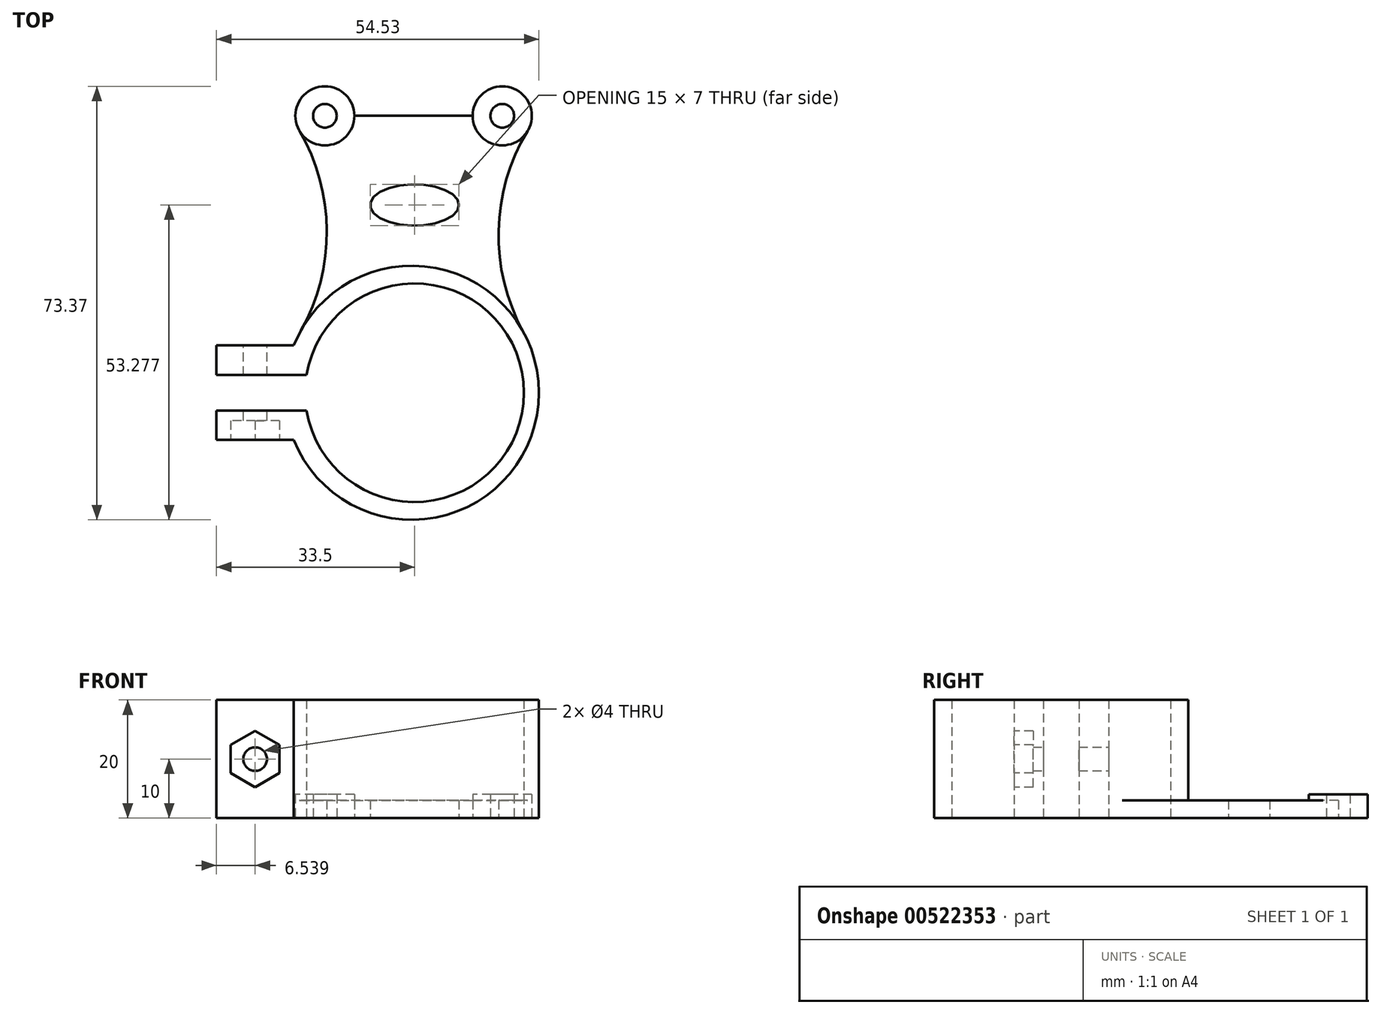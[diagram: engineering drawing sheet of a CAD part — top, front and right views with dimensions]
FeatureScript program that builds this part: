
annotation { "Feature Type Name" : "Feature", "Feature Type Description" : "" }
export const myFeature = defineFeature(function(context is Context, id is Id, definition is map)
    precondition{}
    {
        {
            var Q0;
            Q0=qCreatedBy(makeId("Top.planeOp"),FACE);
            var sketch = newSketch(context, id + "F0", { "sketchPlane" : qUnion([Q0])});
            skArc(sketch, "E0", {"start": v(-18.26, -2.84) * mm, "mid": v(18.5, 0.16) * mm, "end": v(-18.26, 3.16) * mm});
            skLineSegment(sketch, "E1", {"start": v(0, 0) * mm, "end": v(0, -51.02) * mm, "construction": true});
            skLineSegment(sketch, "E2", {"start": v(-15.16, 47.03) * mm, "end": v(14.84, 47.03) * mm});
            skCircle(sketch, "E3", {"center": v(-15.16, 47.03) * mm, "radius": 2 * mm});
            skCircle(sketch, "E4", {"center": v(14.84, 47.03) * mm, "radius": 2 * mm});
            skCircle(sketch, "E5.0", {"center": v(14.84, 47.03) * mm, "radius": 5 * mm});
            skCircle(sketch, "E6.0", {"center": v(-15.16, 47.03) * mm, "radius": 5 * mm});
            skPoint(sketch, "E7.orphan", {"position": v(0, 15) * mm});
            skPoint(sketch, "E8.end.orphan", {"position": v(0, -15) * mm});
            skPoint(sketch, "E9.orphan", {"position": v(0, 21.5) * mm});
            skPoint(sketch, "E10.orphan", {"position": v(0, -21.34) * mm});
            skPoint(sketch, "E11.orphan", {"position": v(-20.16, 47.03) * mm});
            skPoint(sketch, "E12.orphan", {"position": v(19.84, 47.03) * mm});
            skEllipse(sketch, "E13", {"center": v(0, 31.94) * mm, "majorRadius": 7.5 * mm, "minorRadius": 3.5 * mm, "majorAxis": v(1, 0)});
            skLineSegment(sketch, "E14.bottom", {"start": v(-33.5, -5.84) * mm, "end": v(-33.5, -2.84) * mm});
            skPoint(sketch, "E14.middle", {"position": v(-21.5, 0) * mm});
            skLineSegment(sketch, "E15.0", {"start": v(-33.5, 3.16) * mm, "end": v(-21.29, 3.16) * mm});
            skLineSegment(sketch, "E16.0", {"start": v(-33.5, -2.84) * mm, "end": v(-21.29, -2.84) * mm});
            skPoint(sketch, "E17.trimOffspring.end.orphan", {"position": v(-9.5, -6.16) * mm});
            skPoint(sketch, "E18.trimOffspring.end.orphan", {"position": v(-9.5, 5.84) * mm});
            skLineSegment(sketch, "E19.trimOffspring", {"start": v(-33.5, 3.16) * mm, "end": v(-33.5, 6.16) * mm});
            skArc(sketch, "E20.trimOffspring", {"start": v(-20.42, -7.84) * mm, "mid": v(21.03, 0.16) * mm, "end": v(-20.42, 8.16) * mm});
            skLineSegment(sketch, "E21", {"start": v(-21.29, 3.16) * mm, "end": v(-18.26, 3.16) * mm});
            skLineSegment(sketch, "E22", {"start": v(-21.29, -2.84) * mm, "end": v(-18.26, -2.84) * mm});
            skLineSegment(sketch, "E23", {"start": v(-33.5, -5.84) * mm, "end": v(-33.5, -7.84) * mm});
            skLineSegment(sketch, "E24", {"start": v(-33.5, -7.84) * mm, "end": v(-20.42, -7.84) * mm});
            skLineSegment(sketch, "E25", {"start": v(-33.5, 6.16) * mm, "end": v(-33.5, 8.16) * mm});
            skLineSegment(sketch, "E26", {"start": v(-33.5, 8.16) * mm, "end": v(-20.42, 8.16) * mm});
            skPoint(sketch, "E27.endSnap0", {"position": v(-5.46, 31.94) * mm});
            skArc(sketch, "E28", {"start": v(-19.2, 10.7) * mm, "mid": v(-14.84, 27.64) * mm, "end": v(-19.48, 44.51) * mm});
            skArc(sketch, "E29", {"start": v(19.12, 44.44) * mm, "mid": v(14.21, 27.57) * mm, "end": v(18.39, 10.5) * mm});
            skSolve(sketch);
        }
        {
            var Q0;
            Q0=makeQuery(id+"F0.imprint","IMPRINT",FACE,{"disambiguationData":[TD([[makeQuery(id+"F0.imprint","IMPRINT",EDGE,{"derivedFrom":sQuery(id+"F0.wireOp",EDGE,"E0")}),-1.0]])]});
            extrude(context, id + "F1", {"entities" : qUnion([Q0]), "depth" : 20 * mm, "offsetDistance" : 25 * mm});
        }
        {
            var Q0;
            {var subQ1=sQuery(id+"F0.wireOp",EDGE,"a4KQXwT9-HFvs-ruFt-iuDf-gMoE4k8AScbi");Q0=makeQuery(id+"F0.imprint","IMPRINT",FACE,{"disambiguationData":[TD([[makeQuery(id+"F0.imprint","IMPRINT",EDGE,{"derivedFrom":subQ1}),-1.0]])]});}
            var Q1;
            Q1=makeQuery(id+"F0.imprint","IMPRINT",FACE,{"disambiguationData":[TD([[makeQuery(id+"F0.imprint","IMPRINT",EDGE,{"derivedFrom":sQuery(id+"F0.wireOp",EDGE,"E13")}),-1.0]])]});
            var Q2;
            Q2=makeQuery(id+"F0.imprint","IMPRINT",FACE,{"disambiguationData":[TD([[makeQuery(id+"F0.imprint","IMPRINT",EDGE,{"derivedFrom":sQuery(id+"F0.wireOp",EDGE,"E3")}),-1.0]])]});
            var Q3;
            Q3=makeQuery(id+"F0.imprint","IMPRINT",FACE,{"disambiguationData":[TD([[makeQuery(id+"F0.imprint","IMPRINT",EDGE,{"derivedFrom":sQuery(id+"F0.wireOp",EDGE,"E4")}),-1.0]])]});
            extrude(context, id + "F2", {"entities" : qUnion([Q0, Q1, Q2, Q3]), "operationType" : NewBodyOperationType.ADD, "depth" : 3 * mm, "offsetDistance" : 25 * mm});
        }
        {
            var Q0;
            Q0=makeQuery(id+"F0.imprint","IMPRINT",FACE,{"disambiguationData":[TD([[makeQuery(id+"F0.imprint","IMPRINT",EDGE,{"derivedFrom":sQuery(id+"F0.wireOp",EDGE,"E3")}),-1.0]])]});
            var Q1;
            Q1=makeQuery(id+"F0.imprint","IMPRINT",FACE,{"disambiguationData":[TD([[makeQuery(id+"F0.imprint","IMPRINT",EDGE,{"derivedFrom":sQuery(id+"F0.wireOp",EDGE,"E4")}),-1.0]])]});
            extrude(context, id + "F3", {"entities" : qUnion([Q0, Q1]), "operationType" : NewBodyOperationType.ADD, "depth" : 4 * mm, "offsetDistance" : 25 * mm});
        }
        {
            var Q0;
            Q0=makeQuery(id+"F1.opExtrude","SWEPT_FACE",FACE,{"disambiguationData":[OSD([sQuery(id+"F0.wireOp",EDGE,"E24")])]});
            var sketch = newSketch(context, id + "F4", { "sketchPlane" : qUnion([Q0])});
            skCircle(sketch, "E30.cCircle", {"center": v(-26.96, 10) * mm, "radius": 4.12 * mm, "construction": true});
            skPoint(sketch, "E30.cCircle.centerSnap0", {"position": v(-33.5, 10) * mm});
            skPoint(sketch, "E30.cCircle.centerSnap1", {"position": v(-26.96, 0) * mm});
            skLineSegment(sketch, "E30.0", {"start": v(-31.09, 7.62) * mm, "end": v(-31.09, 12.38) * mm});
            skLineSegment(sketch, "E30.1", {"start": v(-31.09, 12.38) * mm, "end": v(-26.96, 14.76) * mm});
            skLineSegment(sketch, "E30.2", {"start": v(-26.96, 14.76) * mm, "end": v(-22.84, 12.38) * mm});
            skLineSegment(sketch, "E30.3", {"start": v(-22.84, 12.38) * mm, "end": v(-22.84, 7.62) * mm});
            skLineSegment(sketch, "E30.4", {"start": v(-22.84, 7.62) * mm, "end": v(-26.96, 5.24) * mm});
            skLineSegment(sketch, "E30.5", {"start": v(-26.96, 5.24) * mm, "end": v(-31.09, 7.62) * mm});
            skPoint(sketch, "E30.0.midPoint", {"position": v(-31.09, 10) * mm});
            skSolve(sketch);
        }
        {
            var Q0;
            Q0=makeQuery(id+"F4.imprint","IMPRINT",FACE,{"disambiguationData":[TD([[makeQuery(id+"F4.imprint","IMPRINT",EDGE,{"derivedFrom":sQuery(id+"F4.wireOp",EDGE,"E30.0")}),-1.0]])]});
            extrude(context, id + "F5", {"entities" : qUnion([Q0]), "operationType" : NewBodyOperationType.REMOVE, "oppositeDirection" : true, "depth" : 3.25 * mm, "offsetDistance" : 25 * mm});
        }
        {
            var Q0;
            Q0=makeQuery(id+"F1.opExtrude","SWEPT_FACE",FACE,{"disambiguationData":[OSD([sQuery(id+"F0.wireOp",EDGE,"E26")])]});
            var sketch = newSketch(context, id + "F6", { "sketchPlane" : qUnion([Q0])});
            skCircle(sketch, "E31", {"center": v(26.96, 10) * mm, "radius": 2 * mm});
            skPoint(sketch, "E31.centerSnap0", {"position": v(33.5, 10) * mm});
            skPoint(sketch, "E31.centerSnap1", {"position": v(26.96, 0) * mm});
            skSolve(sketch);
        }
        {
            var Q0;
            Q0=makeQuery(id+"F6.imprint","IMPRINT",FACE,{"disambiguationData":[TD([[makeQuery(id+"F6.imprint","IMPRINT",EDGE,{"derivedFrom":sQuery(id+"F6.wireOp",EDGE,"E31")}),1.0]])]});
            extrude(context, id + "F7", {"entities" : qUnion([Q0]), "operationType" : NewBodyOperationType.REMOVE, "endBound" : BoundingType.THROUGH_ALL, "oppositeDirection" : true, "depth" : 25 * mm, "offsetDistance" : 25 * mm});
        }
    });
